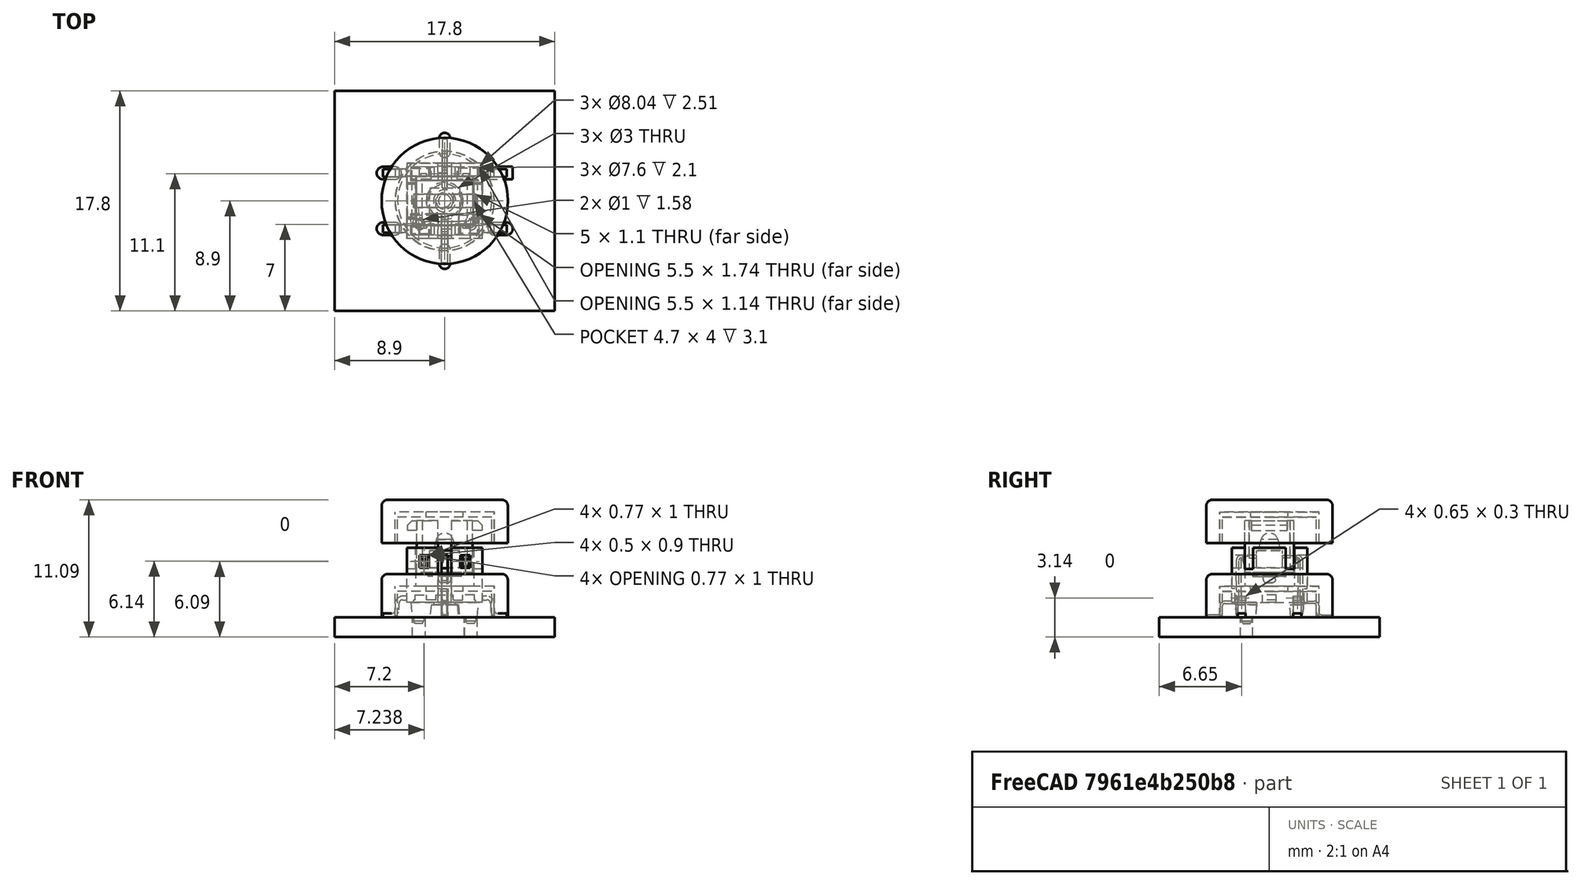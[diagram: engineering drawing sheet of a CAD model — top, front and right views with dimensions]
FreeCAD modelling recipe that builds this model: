
FCSTD DOCUMENT  (FreeCAD 0.17R13541 (Git))
Label: TL3240F160x_TL3240R1CAP
License: All rights reserved
LicenseURL: http://en.wikipedia.org/wiki/All_rights_reserved
objects: Part::FeaturePython×5, Part::Feature×5, Part::Cylinder×5, Part::Cut×2, App::Part×2, App::DocumentObjectGroup×1, Part::Fillet×1, Part::Fuse×1
note: 19 computed .brp shape members not serialized (recipe doc carries the construction recipe); baked Part::Feature solids carry a one-line shape summary decoded from their .brp

FEATURE [Part::FeaturePython] FCrtYd_lines  label="FCrtYd"  # a2plus imported part (geometry in sourceFile) (typed FeaturePython)
  fixedPosition = true
FEATURE [Part::FeaturePython] Filk_lines  label="FrontSilk"  # a2plus imported part (geometry in sourceFile) (typed FeaturePython)
  fixedPosition = true
FEATURE [Part::FeaturePython] TopPads  # a2plus imported part (geometry in sourceFile) (typed FeaturePython)
  fixedPosition = true
FEATURE [Part::FeaturePython] THPs  label="PTHs"  # a2plus imported part (geometry in sourceFile) (typed FeaturePython)
  fixedPosition = true
FEATURE [Part::FeaturePython] newPCB  label="Pcb"  # a2plus imported part (geometry in sourceFile) (typed FeaturePython)
  fixedPosition = true
FEATURE [App::DocumentObjectGroup] E_Switch_SPST_LED_RoundCap_TL3240F160x_fp
  Group = -> [FCrtYd_lines,Filk_lines,TopPads,THPs,newPCB]
FEATURE [Part::Feature] Part__Feature  label="TL3240xxxx"
  Placement = pos=(0,0,1) rot=(0,0,1;3.14159rad)
  shape: bbox 10.01 x 10.01 x 8.308 mm, 263 faces (baked)
FEATURE [Part::Cylinder] Cylinder
  Angle = 360
  AttacherType = Attacher::AttachEngine3D
  Height = 3.5
  Radius = 5.1
FEATURE [Part::Cylinder] Cylinder003
  Angle = 360
  AttacherType = Attacher::AttachEngine3D
  Height = 2.1
  Radius = 3.8
FEATURE [Part::Cylinder] Cylinder001
  Angle = 360
  AttacherType = Attacher::AttachEngine3D
  Height = 2.51
  Radius = 4.02
FEATURE [Part::Cut] Cut
  Base = -> Cylinder
  Tool = -> Cylinder001
FEATURE [Part::Fillet] Fillet
  Base = -> Cut
  Edges = 1 edges r=0.5: [Edge1]
FEATURE [Part::Cylinder] Cylinder004
  Angle = 360
  AttacherType = Attacher::AttachEngine3D
  Height = 3
  Radius = 1.5
FEATURE [Part::Fuse] Fusion
  Base = -> Cylinder003
  Tool = -> Cylinder004
FEATURE [Part::Cylinder] Cylinder002
  Angle = 360
  AttacherType = Attacher::AttachEngine3D
  Height = 2.5
  Radius = 4
FEATURE [Part::Cut] Cut001
  Base = -> Cylinder002
  Tool = -> Fusion
FEATURE [App::Part] Part001
  Group = -> [Cylinder001,Cylinder,Cut,Fillet,Cylinder002,Fusion,Cylinder004,Cylinder003,Cut001]
  License = CC BY 3.0
  LicenseURL = http://creativecommons.org/licenses/by/3.0/
  Origin = -> Origin001
  Placement = pos=(0,0,6) rot=(0,0,1;0rad)
FEATURE [App::Part] Part  label="TL3240xxxx_TL3240R1CAP"
  Group = -> [Part__Feature,Part001]
  License = CC BY 3.0
  LicenseURL = http://creativecommons.org/licenses/by/3.0/
  Origin = -> Origin
FEATURE [Part::Feature] Part__Feature_cp  label="TL3240xxxx_cp"
  Placement = pos=(0,0,1) rot=(0,0,1;3.14159rad)
  shape: bbox 10.01 x 10.01 x 8.308 mm, 263 faces (baked)
FEATURE [Part::Feature] Fillet_cp
  Placement = pos=(0,0,6) rot=(0,0,1;0rad)
  shape: bbox 11.04 x 11.04 x 3.5 mm, 6 faces (baked)
FEATURE [Part::Feature] Cut001_cp
  Placement = pos=(0,0,6) rot=(0,0,1;0rad)
  shape: bbox 8 x 8 x 2.5 mm, 6 faces (baked)
FEATURE [Part::Feature] Shape  label="TL3240xxxx_TL3240R1CAP_cp"
  shape: bbox 11.05 x 11.05 x 10.01 mm, 275 faces, 3 solids (baked)
